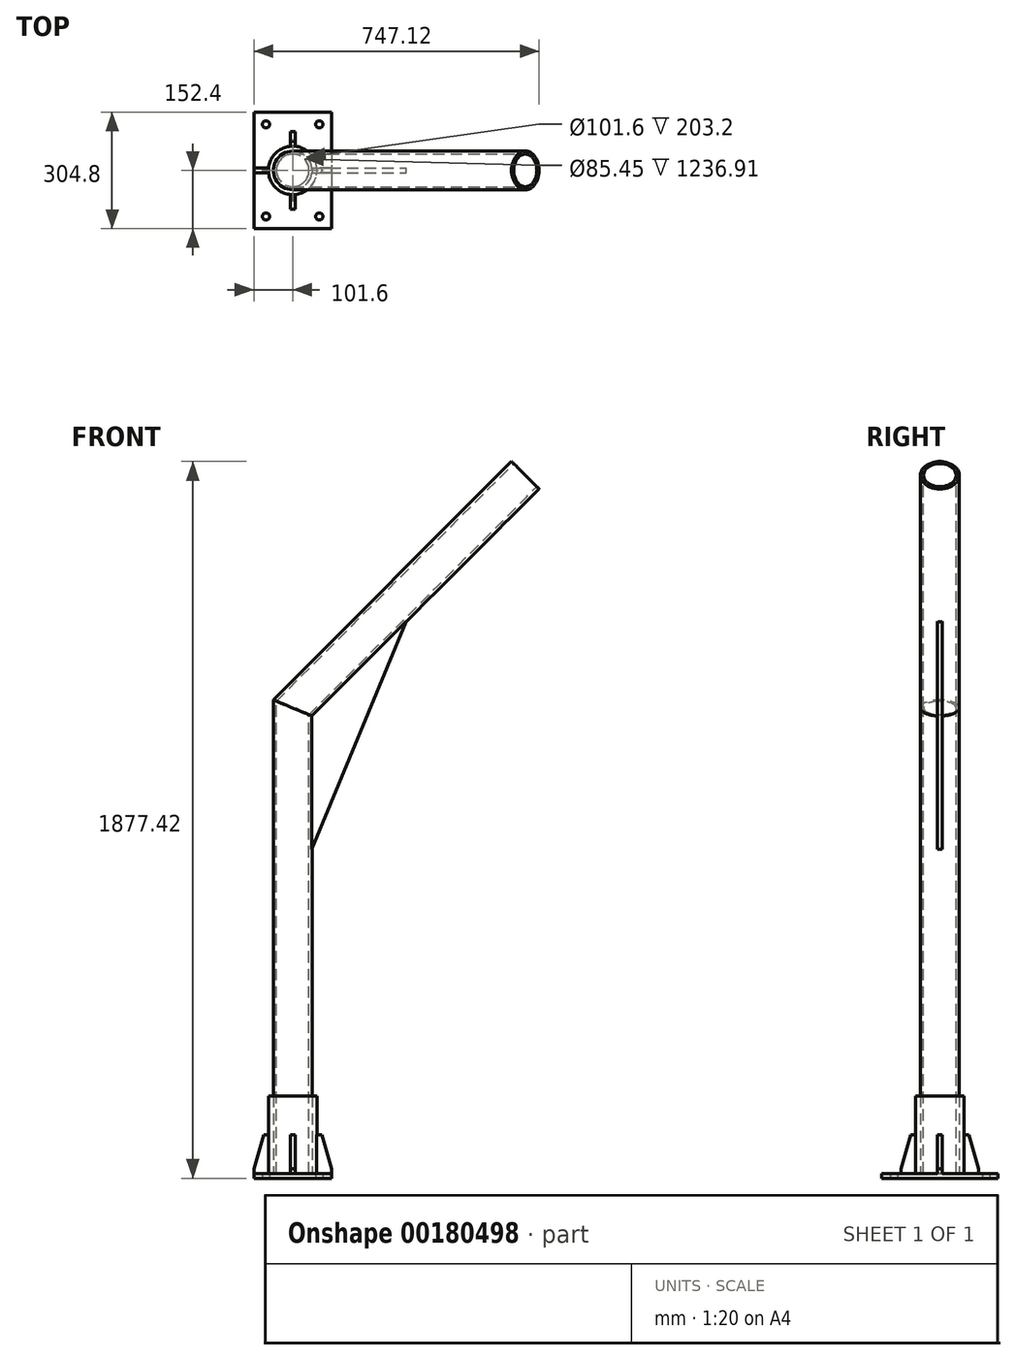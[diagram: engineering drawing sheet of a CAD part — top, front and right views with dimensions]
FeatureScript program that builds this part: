
annotation { "Feature Type Name" : "Feature", "Feature Type Description" : "" }
export const myFeature = defineFeature(function(context is Context, id is Id, definition is map)
    precondition{}
    {
        {
            var Q0;
            Q0=qCreatedBy(makeId("Top.planeOp"),FACE);
            var sketch = newSketch(context, id + "F0", { "sketchPlane" : qUnion([Q0])});
            skLineSegment(sketch, "E0.bottom", {"start": v(101.6, 152.4) * mm, "end": v(-101.6, 152.4) * mm});
            skLineSegment(sketch, "E0.top", {"start": v(101.6, -152.4) * mm, "end": v(-101.6, -152.4) * mm});
            skLineSegment(sketch, "E0.left", {"start": v(101.6, 152.4) * mm, "end": v(101.6, -152.4) * mm});
            skLineSegment(sketch, "E0.right", {"start": v(-101.6, 152.4) * mm, "end": v(-101.6, -152.4) * mm});
            skPoint(sketch, "E0.middle", {"position": v(0, 0) * mm});
            skCircle(sketch, "E1", {"center": v(-69.85, 120.65) * mm, "radius": 9.53 * mm});
            skLineSegment(sketch, "E2", {"start": v(0, 0) * mm, "end": v(0, 37.42) * mm, "construction": true});
            skLineSegment(sketch, "E3", {"start": v(0, 0) * mm, "end": v(35.12, 0) * mm, "construction": true});
            skCircle(sketch, "E4.MirrorC", {"center": v(69.85, 120.65) * mm, "radius": 9.53 * mm});
            skCircle(sketch, "E5.MirrorC", {"center": v(69.85, -120.65) * mm, "radius": 9.53 * mm});
            skCircle(sketch, "E6.MirrorC", {"center": v(-69.85, -120.65) * mm, "radius": 9.53 * mm});
            skSolve(sketch);
        }
        {
            var Q0;
            Q0 = qSketchRegion(id + "F0", true);
            extrude(context, id + "F1", {"entities" : qUnion([Q0]), "depth" : 12.7 * mm});
        }
        {
            var Q0;
            Q0=makeQuery(id+"F1.opExtrude","CAP_FACE",FACE,{"disambiguationData":[OSD([sQuery(id+"F0.wireOp",EDGE,"E0.bottom"),sQuery(id+"F0.wireOp",EDGE,"E0.top"),sQuery(id+"F0.wireOp",EDGE,"E0.left"),sQuery(id+"F0.wireOp",EDGE,"E0.right"),sQuery(id+"F0.wireOp",EDGE,"E1"),sQuery(id+"F0.wireOp",EDGE,"E4.MirrorC"),sQuery(id+"F0.wireOp",EDGE,"E5.MirrorC"),sQuery(id+"F0.wireOp",EDGE,"E6.MirrorC")])],"isStart":false});
            var sketch = newSketch(context, id + "F2", { "sketchPlane" : qUnion([Q0])});
            skCircle(sketch, "E7", {"center": v(0, 0) * mm, "radius": 50.8 * mm});
            skCircle(sketch, "E8", {"center": v(0, 0) * mm, "radius": 63.5 * mm});
            skSolve(sketch);
        }
        {
            var Q0;
            Q0 = qSketchRegion(id + "F2", true);
            extrude(context, id + "F3", {"entities" : qUnion([Q0]), "operationType" : NewBodyOperationType.ADD, "depth" : 203.2 * mm});
        }
        {
            var Q0;
            Q0=qCreatedBy(makeId("Front.planeOp"),FACE);
            var sketch = newSketch(context, id + "F4", { "sketchPlane" : qUnion([Q0])});
            skLineSegment(sketch, "E9", {"start": v(0, 12.7) * mm, "end": v(0, 1231.9) * mm});
            skLineSegment(sketch, "E10", {"start": v(0, 1231.9) * mm, "end": v(609.6, 1841.5) * mm});
            skSolve(sketch);
        }
        {
            var Q0;
            Q0=makeQuery(id+"F1.opExtrude","CAP_FACE",FACE,{"disambiguationData":[OSD([sQuery(id+"F0.wireOp",EDGE,"E0.bottom"),sQuery(id+"F0.wireOp",EDGE,"E0.top"),sQuery(id+"F0.wireOp",EDGE,"E0.left"),sQuery(id+"F0.wireOp",EDGE,"E0.right")])],"isStart":false});
            var sketch = newSketch(context, id + "F5", { "sketchPlane" : qUnion([Q0])});
            skCircle(sketch, "E11", {"center": v(0, 0) * mm, "radius": 50.8 * mm});
            skCircle(sketch, "E12", {"center": v(0, 0) * mm, "radius": 42.72 * mm});
            skSolve(sketch);
        }
        {
            var Q0;
            Q0 = qSketchRegion(id + "F5", true);
            var Q1;
            Q1 = qConstructionFilter(qBodyType(qCreatedBy(id + "F4" ,EDGE), BodyType.WIRE), ConstructionObject.NO);
            sweep(context, id + "F6", {"profiles" : qUnion([Q0]), "path" : qUnion([Q1])});
        }
        {
            var Q0;
            Q0=qCreatedBy(makeId("Front.planeOp"),FACE);
            var sketch = newSketch(context, id + "F7", { "sketchPlane" : qUnion([Q0])});
            skLineSegment(sketch, "E13", {"start": v(645.52, 1805.58) * mm, "end": v(50.8, 1210.86) * mm, "construction": true});
            skLineSegment(sketch, "E14", {"start": v(50.8, 1210.86) * mm, "end": v(50.8, 12.7) * mm, "construction": true});
            skLineSegment(sketch, "E15", {"start": v(48.26, 1211.91) * mm, "end": v(299.7, 1463.36) * mm});
            skLineSegment(sketch, "E16", {"start": v(299.7, 1463.36) * mm, "end": v(48.26, 856.31) * mm});
            skLineSegment(sketch, "E17", {"start": v(48.26, 856.31) * mm, "end": v(48.26, 1211.91) * mm});
            skLineSegment(sketch, "E18", {"start": v(50.8, 1210.86) * mm, "end": v(49, 1212.65) * mm, "construction": true});
            skLineSegment(sketch, "E19", {"start": v(50.8, 1210.86) * mm, "end": v(48.26, 1210.86) * mm, "construction": true});
            skSolve(sketch);
        }
        {
            var Q0;
            Q0 = qSketchRegion(id + "F7", true);
            extrude(context, id + "F8", {"entities" : qUnion([Q0]), "operationType" : NewBodyOperationType.ADD, "endBound" : BoundingType.SYMMETRIC, "depth" : 12.7 * mm});
        }
        {
            var Q0;
            Q0=qCreatedBy(makeId("Front.planeOp"),FACE);
            var sketch = newSketch(context, id + "F9", { "sketchPlane" : qUnion([Q0])});
            skLineSegment(sketch, "E20.0", {"start": v(101.6, 12.7) * mm, "end": v(-101.6, 12.7) * mm, "construction": true});
            skLineSegment(sketch, "E21", {"start": v(63.5, 114.3) * mm, "end": v(76.2, 114.3) * mm});
            skLineSegment(sketch, "E22", {"start": v(76.2, 114.3) * mm, "end": v(101.6, 25.4) * mm});
            skLineSegment(sketch, "E23", {"start": v(101.6, 25.4) * mm, "end": v(101.6, 12.7) * mm});
            skLineSegment(sketch, "E24", {"start": v(63.5, 12.7) * mm, "end": v(101.6, 12.7) * mm});
            skLineSegment(sketch, "E25.bottom", {"start": v(63.5, 114.3) * mm, "end": v(60.96, 114.3) * mm});
            skLineSegment(sketch, "E25.top", {"start": v(63.5, 12.7) * mm, "end": v(60.96, 12.7) * mm});
            skLineSegment(sketch, "E25.left", {"start": v(63.5, 114.3) * mm, "end": v(63.5, 12.7) * mm, "construction": true});
            skLineSegment(sketch, "E25.right", {"start": v(60.96, 114.3) * mm, "end": v(60.96, 12.7) * mm});
            skLineSegment(sketch, "E26.0", {"start": v(-63.5, 215.9) * mm, "end": v(63.5, 215.9) * mm, "construction": true});
            skLineSegment(sketch, "E27", {"start": v(63.5, 215.9) * mm, "end": v(63.5, 114.3) * mm, "construction": true});
            skSolve(sketch);
        }
        {
            var Q0;
            Q0 = qSketchRegion(id + "F9", true);
            extrude(context, id + "F10", {"entities" : qUnion([Q0]), "endBound" : BoundingType.SYMMETRIC, "depth" : 12.7 * mm});
        }
        {
            var Q0;
            Q0=makeQuery(id+"F10.opExtrude","SWEPT_BODY",BODY,{"disambiguationData":[OSD([sQuery(id+"F9.wireOp",EDGE,"E21"),sQuery(id+"F9.wireOp",EDGE,"E22"),sQuery(id+"F9.wireOp",EDGE,"E23"),sQuery(id+"F9.wireOp",EDGE,"E24"),sQuery(id+"F9.wireOp",EDGE,"E25.bottom"),sQuery(id+"F9.wireOp",EDGE,"E25.top"),sQuery(id+"F9.wireOp",EDGE,"E25.right")])]});
            var Q1;
            Q1=makeQuery(id+"F3.opExtrude","SWEPT_FACE",FACE,{"disambiguationData":[OSD([sQuery(id+"F2.wireOp",EDGE,"E8")])]});
            circularPattern(context, id + "F11", {"operationType" : NewBodyOperationType.ADD, "entities" : qUnion([Q0]), "axis" : qUnion([Q1]), "angle" : 360 * degree, "instanceCount" : 4, "equalSpace" : true});
        }
    });
